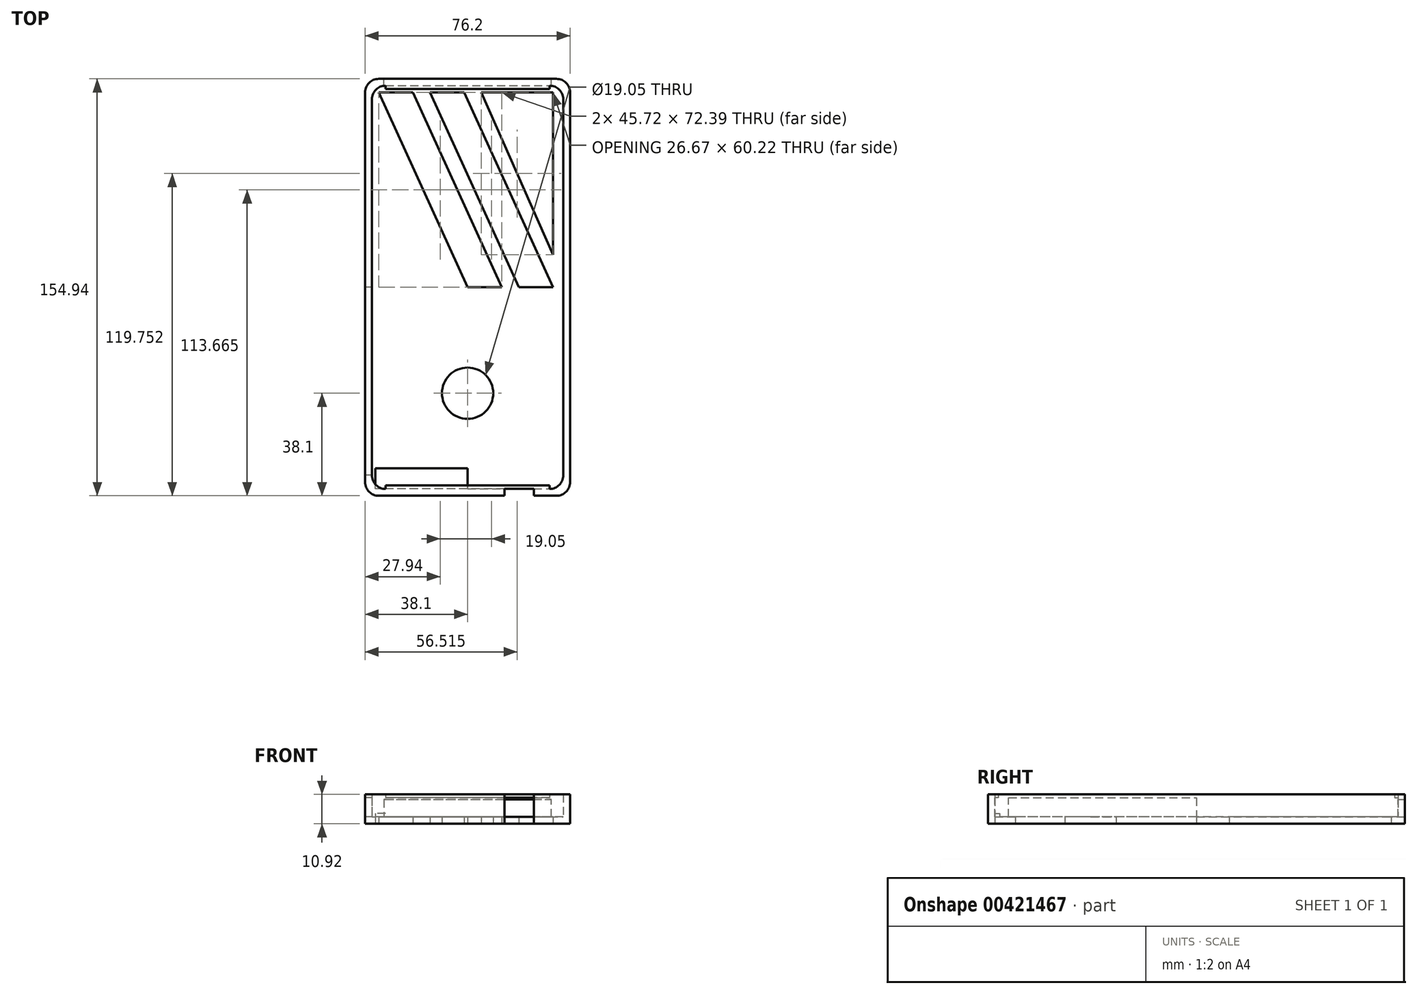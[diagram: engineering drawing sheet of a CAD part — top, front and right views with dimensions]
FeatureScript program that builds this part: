
annotation { "Feature Type Name" : "Feature", "Feature Type Description" : "" }
export const myFeature = defineFeature(function(context is Context, id is Id, definition is map)
    precondition{}
    {
        {
            var Q0;
            Q0=qCreatedBy(makeId("Top.planeOp"),FACE);
            var sketch = newSketch(context, id + "F0", { "sketchPlane" : qUnion([Q0])});
            skLineSegment(sketch, "E0", {"start": v(0, 0) * mm, "end": v(76.2, 0) * mm});
            skLineSegment(sketch, "E1", {"start": v(0, 0) * mm, "end": v(0, 154.94) * mm});
            skLineSegment(sketch, "E2", {"start": v(0, 154.94) * mm, "end": v(76.2, 154.94) * mm});
            skLineSegment(sketch, "E3", {"start": v(76.2, 154.94) * mm, "end": v(76.2, 0) * mm});
            skSolve(sketch);
        }
        {
            var Q0;
            Q0=makeQuery(id+"F0.imprint","IMPRINT",FACE,{"disambiguationData":[TD([[makeQuery(id+"F0.imprint","IMPRINT",EDGE,{"derivedFrom":sQuery(id+"F0.wireOp",EDGE,"E0")}),1.0]])]});
            extrude(context, id + "F1", {"entities" : qUnion([Q0]), "depth" : 10.92 * mm});
        }
        {
            var Q0;
            Q0=makeQuery(id+"F1.opExtrude","CAP_FACE",FACE,{"disambiguationData":[OSD([sQuery(id+"F0.wireOp",EDGE,"E0"),sQuery(id+"F0.wireOp",EDGE,"E1"),sQuery(id+"F0.wireOp",EDGE,"E2"),sQuery(id+"F0.wireOp",EDGE,"E3")])],"isStart":false});
            shell(context, id + "F2", {"entities" : qUnion([Q0]), "thickness" : 2.54 * mm});
        }
        {
            var Q0;
            Q0=makeQuery(id+"F1.opExtrude","SWEPT_EDGE",EDGE,{"disambiguationData":[OSD([sQuery(id+"F0.wireOp",EDGE,"E1"),sQuery(id+"F0.wireOp",EDGE,"E2")])]});
            var Q1;
            Q1=makeQuery(id+"F1.opExtrude","SWEPT_EDGE",EDGE,{"disambiguationData":[OSD([sQuery(id+"F0.wireOp",EDGE,"E2"),sQuery(id+"F0.wireOp",EDGE,"E3")])]});
            var Q2;
            Q2=makeQuery(id+"F1.opExtrude","SWEPT_EDGE",EDGE,{"disambiguationData":[OSD([sQuery(id+"F0.wireOp",EDGE,"E0"),sQuery(id+"F0.wireOp",EDGE,"E3")])]});
            var Q3;
            Q3=makeQuery(id+"F1.opExtrude","SWEPT_EDGE",EDGE,{"disambiguationData":[OSD([sQuery(id+"F0.wireOp",EDGE,"E0"),sQuery(id+"F0.wireOp",EDGE,"E1")])]});
            var Q4;
            Q4=makeQuery(id+"F2.opShell","OFFSET_EDGE",EDGE,{"disambiguationData":[OSD([sQuery(id+"F0.wireOp",EDGE,"E0"),sQuery(id+"F0.wireOp",EDGE,"E1")])]});
            var Q5;
            Q5=makeQuery(id+"F2.opShell","OFFSET_EDGE",EDGE,{"disambiguationData":[OSD([sQuery(id+"F0.wireOp",EDGE,"E0"),sQuery(id+"F0.wireOp",EDGE,"E3")])]});
            var Q6;
            Q6=makeQuery(id+"F2.opShell","OFFSET_EDGE",EDGE,{"disambiguationData":[OSD([sQuery(id+"F0.wireOp",EDGE,"E2"),sQuery(id+"F0.wireOp",EDGE,"E3")])]});
            var Q7;
            Q7=makeQuery(id+"F2.opShell","OFFSET_EDGE",EDGE,{"disambiguationData":[OSD([sQuery(id+"F0.wireOp",EDGE,"E1"),sQuery(id+"F0.wireOp",EDGE,"E2")])]});
            fillet(context, id + "F3", {"entities" : qUnion([Q0, Q1, Q2, Q3, Q4, Q5, Q6, Q7]), "radius" : 5.08 * mm, "tangentPropagation" : true, "allowEdgeOverflow" : false});
        }
        {
            var Q0;
            Q0=makeQuery(id+"F2.opShell","OFFSET_FACE",FACE,{"disambiguationData":[OSD([sQuery(id+"F0.wireOp",EDGE,"E2")])]});
            var sketch = newSketch(context, id + "F4", { "sketchPlane" : qUnion([Q0])});
            skLineSegment(sketch, "E4", {"start": v(7.62, 10.92) * mm, "end": v(7.62, 9.64) * mm});
            skLineSegment(sketch, "E5", {"start": v(7.62, 9.64) * mm, "end": v(68.58, 9.64) * mm});
            skLineSegment(sketch, "E6", {"start": v(68.58, 9.64) * mm, "end": v(68.58, 10.92) * mm});
            skLineSegment(sketch, "E7", {"start": v(68.58, 10.92) * mm, "end": v(7.62, 10.92) * mm});
            skSolve(sketch);
        }
        {
            var Q0;
            Q0=makeQuery(id+"F4.imprint","IMPRINT",FACE,{"disambiguationData":[TD([[makeQuery(id+"F4.imprint","IMPRINT",EDGE,{"derivedFrom":sQuery(id+"F4.wireOp",EDGE,"E4")}),1.0]])]});
            extrude(context, id + "F5", {"entities" : qUnion([Q0]), "operationType" : NewBodyOperationType.ADD, "depth" : 1.27 * mm});
        }
        {
            var Q0;
            Q0=makeQuery(id+"F2.opShell","OFFSET_FACE",FACE,{"disambiguationData":[OSD([sQuery(id+"F0.wireOp",EDGE,"E0")])]});
            var sketch = newSketch(context, id + "F6", { "sketchPlane" : qUnion([Q0])});
            skLineSegment(sketch, "E8", {"start": v(-68.58, 10.92) * mm, "end": v(-68.58, 9.66) * mm});
            skLineSegment(sketch, "E9", {"start": v(-68.58, 9.66) * mm, "end": v(-7.62, 9.66) * mm});
            skLineSegment(sketch, "E10", {"start": v(-7.62, 9.66) * mm, "end": v(-7.62, 10.92) * mm});
            skLineSegment(sketch, "E11", {"start": v(-7.62, 10.92) * mm, "end": v(-68.58, 10.92) * mm});
            skSolve(sketch);
        }
        {
            var Q0;
            Q0=makeQuery(id+"F6.imprint","IMPRINT",FACE,{"disambiguationData":[TD([[makeQuery(id+"F6.imprint","IMPRINT",EDGE,{"derivedFrom":sQuery(id+"F6.wireOp",EDGE,"E8")}),1.0]])]});
            extrude(context, id + "F7", {"entities" : qUnion([Q0]), "operationType" : NewBodyOperationType.ADD, "depth" : 1.27 * mm});
        }
        {
            var Q0;
            Q0=makeQuery(id+"F1.opExtrude","CAP_FACE",FACE,{"disambiguationData":[OSD([sQuery(id+"F0.wireOp",EDGE,"E0"),sQuery(id+"F0.wireOp",EDGE,"E1"),sQuery(id+"F0.wireOp",EDGE,"E2"),sQuery(id+"F0.wireOp",EDGE,"E3")])],"isStart":true});
            var sketch = newSketch(context, id + "F8", { "sketchPlane" : qUnion([Q0])});
            skLineSegment(sketch, "E12", {"start": v(38.1, 0) * mm, "end": v(38.1, -38.1) * mm, "construction": true});
            skCircle(sketch, "E13", {"center": v(38.1, -38.1) * mm, "radius": 9.53 * mm});
            skLineSegment(sketch, "E14", {"start": v(38.1, -2.54) * mm, "end": v(38.1, 0) * mm});
            skLineSegment(sketch, "E15", {"start": v(38.1, -2.54) * mm, "end": v(3.8, -2.54) * mm});
            skLineSegment(sketch, "E16", {"start": v(3.8, -2.54) * mm, "end": v(3.8, -10.16) * mm});
            skLineSegment(sketch, "E17", {"start": v(3.8, -10.16) * mm, "end": v(38.1, -10.16) * mm});
            skLineSegment(sketch, "E18", {"start": v(38.1, -10.16) * mm, "end": v(38.1, -2.54) * mm});
            skSolve(sketch);
        }
        {
            var Q0;
            Q0=makeQuery(id+"F8.imprint","IMPRINT",FACE,{"disambiguationData":[TD([[makeQuery(id+"F8.imprint","IMPRINT",EDGE,{"derivedFrom":sQuery(id+"F8.wireOp",EDGE,"E15")}),1.0]])]});
            var Q1;
            Q1=makeQuery(id+"F8.imprint","IMPRINT",FACE,{"disambiguationData":[TD([[makeQuery(id+"F8.imprint","IMPRINT",EDGE,{"derivedFrom":sQuery(id+"F8.wireOp",EDGE,"E13")}),1.0]])]});
            extrude(context, id + "F9", {"entities" : qUnion([Q0, Q1]), "operationType" : NewBodyOperationType.REMOVE, "oppositeDirection" : true, "depth" : 3.8 * mm});
        }
        {
            var Q0;
            Q0=makeQuery(id+"F1.opExtrude","SWEPT_FACE",FACE,{"disambiguationData":[OSD([sQuery(id+"F0.wireOp",EDGE,"E0")])]});
            var sketch = newSketch(context, id + "F10", { "sketchPlane" : qUnion([Q0])});
            skLineSegment(sketch, "E19", {"start": v(51.75, 0) * mm, "end": v(51.75, 10.92) * mm});
            skLineSegment(sketch, "E20", {"start": v(51.75, 10.92) * mm, "end": v(62.67, 10.92) * mm});
            skLineSegment(sketch, "E21", {"start": v(62.67, 10.92) * mm, "end": v(62.67, 0) * mm});
            skLineSegment(sketch, "E22", {"start": v(62.67, 0) * mm, "end": v(51.75, 0) * mm});
            skSolve(sketch);
        }
        {
            var Q0;
            Q0=makeQuery(id+"F10.imprint","IMPRINT",FACE,{"disambiguationData":[TD([[makeQuery(id+"F10.imprint","IMPRINT",EDGE,{"derivedFrom":sQuery(id+"F10.wireOp",EDGE,"E19")}),-1.0]])]});
            extrude(context, id + "F11", {"entities" : qUnion([Q0]), "operationType" : NewBodyOperationType.REMOVE, "oppositeDirection" : true, "depth" : 2.54 * mm});
        }
        {
            var Q0;
            Q0=makeQuery(id+"F1.opExtrude","SWEPT_FACE",FACE,{"disambiguationData":[OSD([sQuery(id+"F0.wireOp",EDGE,"E2")])]});
            var sketch = newSketch(context, id + "F12", { "sketchPlane" : qUnion([Q0])});
            skLineSegment(sketch, "E23", {"start": v(-71.12, 0) * mm, "end": v(-69.21, 0) * mm, "construction": true});
            skLineSegment(sketch, "E24", {"start": v(-69.21, 0) * mm, "end": v(-69.21, 2.54) * mm, "construction": true});
            skLineSegment(sketch, "E25", {"start": v(-71.12, 10.92) * mm, "end": v(-69.21, 10.92) * mm, "construction": true});
            skLineSegment(sketch, "E26", {"start": v(-69.21, 10.92) * mm, "end": v(-69.21, 9.02) * mm, "construction": true});
            skLineSegment(sketch, "E27", {"start": v(-5.08, 0) * mm, "end": v(-6.98, 0) * mm, "construction": true});
            skLineSegment(sketch, "E28", {"start": v(-6.98, 0) * mm, "end": v(-6.98, 2.54) * mm, "construction": true});
            skLineSegment(sketch, "E29", {"start": v(-5.08, 10.92) * mm, "end": v(-6.99, 10.92) * mm, "construction": true});
            skLineSegment(sketch, "E30", {"start": v(-6.99, 10.92) * mm, "end": v(-6.99, 9.02) * mm, "construction": true});
            skLineSegment(sketch, "E31", {"start": v(-69.21, 2.54) * mm, "end": v(-69.21, 9.02) * mm});
            skLineSegment(sketch, "E32", {"start": v(-6.99, 9.02) * mm, "end": v(-69.21, 9.02) * mm});
            skLineSegment(sketch, "E33", {"start": v(-6.99, 9.02) * mm, "end": v(-6.98, 2.54) * mm});
            skLineSegment(sketch, "E34", {"start": v(-6.98, 2.54) * mm, "end": v(-69.21, 2.54) * mm});
            skSolve(sketch);
        }
        {
            var Q0;
            Q0=makeQuery(id+"F12.imprint","IMPRINT",FACE,{"disambiguationData":[TD([[makeQuery(id+"F12.imprint","IMPRINT",EDGE,{"derivedFrom":sQuery(id+"F12.wireOp",EDGE,"E31")}),-1.0]])]});
            extrude(context, id + "F13", {"entities" : qUnion([Q0]), "operationType" : NewBodyOperationType.REMOVE, "oppositeDirection" : true, "depth" : 3.8 * mm});
        }
        {
            var Q0;
            Q0=makeQuery(id+"F1.opExtrude","SWEPT_FACE",FACE,{"disambiguationData":[OSD([sQuery(id+"F0.wireOp",EDGE,"E1")])]});
            var sketch = newSketch(context, id + "F14", { "sketchPlane" : qUnion([Q0])});
            skLineSegment(sketch, "E35", {"start": v(-77.47, 2.54) * mm, "end": v(-7.62, 2.54) * mm});
            skPoint(sketch, "E35.startSnap0", {"position": v(-77.47, 0) * mm});
            skLineSegment(sketch, "E36", {"start": v(-7.62, 2.54) * mm, "end": v(-7.62, 9.65) * mm});
            skLineSegment(sketch, "E37", {"start": v(-7.62, 9.65) * mm, "end": v(-77.47, 9.65) * mm});
            skLineSegment(sketch, "E38", {"start": v(-77.47, 9.65) * mm, "end": v(-77.47, 2.54) * mm});
            skSolve(sketch);
        }
        {
            var Q0;
            Q0=makeQuery(id+"F14.imprint","IMPRINT",FACE,{"disambiguationData":[TD([[makeQuery(id+"F14.imprint","IMPRINT",EDGE,{"derivedFrom":sQuery(id+"F14.wireOp",EDGE,"E35")}),1.0]])]});
            extrude(context, id + "F15", {"entities" : qUnion([Q0]), "operationType" : NewBodyOperationType.REMOVE, "oppositeDirection" : true, "depth" : 2.54 * mm});
        }
        {
            var Q0;
            Q0=makeQuery(id+"F1.opExtrude","CAP_FACE",FACE,{"disambiguationData":[OSD([sQuery(id+"F0.wireOp",EDGE,"E0"),sQuery(id+"F0.wireOp",EDGE,"E1"),sQuery(id+"F0.wireOp",EDGE,"E2"),sQuery(id+"F0.wireOp",EDGE,"E3")])],"isStart":true});
            var sketch = newSketch(context, id + "F16", { "sketchPlane" : qUnion([Q0])});
            skLineSegment(sketch, "E39", {"start": v(5.08, -149.86) * mm, "end": v(38.1, -77.47) * mm});
            skPoint(sketch, "E39.endSnap0", {"position": v(38.1, -154.94) * mm});
            skPoint(sketch, "E39.endSnap1", {"position": v(0, -77.47) * mm});
            skLineSegment(sketch, "E40", {"start": v(38.1, -77.47) * mm, "end": v(50.8, -77.47) * mm});
            skLineSegment(sketch, "E41", {"start": v(50.8, -77.47) * mm, "end": v(17.78, -149.86) * mm});
            skLineSegment(sketch, "E42", {"start": v(5.08, -149.86) * mm, "end": v(17.78, -149.86) * mm});
            skLineSegment(sketch, "E43", {"start": v(57.15, -77.47) * mm, "end": v(24.13, -149.86) * mm});
            skLineSegment(sketch, "E44", {"start": v(24.13, -149.86) * mm, "end": v(36.83, -149.86) * mm});
            skLineSegment(sketch, "E45", {"start": v(36.83, -149.86) * mm, "end": v(69.85, -77.47) * mm});
            skLineSegment(sketch, "E46", {"start": v(69.85, -77.47) * mm, "end": v(57.15, -77.47) * mm});
            skPoint(sketch, "E47.startSnap0", {"position": v(30.48, -149.86) * mm});
            skLineSegment(sketch, "E48", {"start": v(69.85, -89.64) * mm, "end": v(43.18, -149.86) * mm});
            skLineSegment(sketch, "E49", {"start": v(43.18, -149.86) * mm, "end": v(69.85, -149.86) * mm});
            skLineSegment(sketch, "E50", {"start": v(69.85, -149.86) * mm, "end": v(69.85, -89.64) * mm});
            skSolve(sketch);
        }
        {
            var Q0;
            Q0=makeQuery(id+"F16.imprint","IMPRINT",FACE,{"disambiguationData":[TD([[makeQuery(id+"F16.imprint","IMPRINT",EDGE,{"derivedFrom":sQuery(id+"F16.wireOp",EDGE,"E39")}),-1.0]])]});
            var Q1;
            Q1=makeQuery(id+"F16.imprint","IMPRINT",FACE,{"disambiguationData":[TD([[makeQuery(id+"F16.imprint","IMPRINT",EDGE,{"derivedFrom":sQuery(id+"F16.wireOp",EDGE,"E43")}),1.0]])]});
            var Q2;
            Q2=makeQuery(id+"F16.imprint","IMPRINT",FACE,{"disambiguationData":[TD([[makeQuery(id+"F16.imprint","IMPRINT",EDGE,{"derivedFrom":sQuery(id+"F16.wireOp",EDGE,"E48")}),1.0]])]});
            extrude(context, id + "F17", {"entities" : qUnion([Q0, Q1, Q2]), "operationType" : NewBodyOperationType.REMOVE, "oppositeDirection" : true, "depth" : 2.54 * mm});
        }
    });
